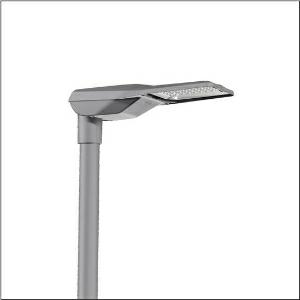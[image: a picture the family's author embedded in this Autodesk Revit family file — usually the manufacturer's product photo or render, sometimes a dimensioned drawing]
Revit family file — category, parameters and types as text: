
# Revit family: streetlight_sl_21_iq_mini___st1_5a_5xe2p41g08hb_3230
name_source: partatom
category: Lighting Fixtures
units: mm (PartAtom-declared; Revit-internal decimal feet)

## family parameters
Cut with Voids When Loaded = No
Host = Face
Light Source = No
Part Type = Normal
Room Calculation Point = No
Round Connector Dimension = Use Diameter
Shared = No

## types (1)
- --- (1 x LED, 9690 lm, 70.9 W, 4000K)
    Apparent Load = 71 VA
    CIE Flux Codes = 22 53 95 100 100
    Color Rendering = 70
    Color Temperature = 4000K
    Default Elevation = 1800 mm
    Description = Streetlight SL 21 mini, mast luminaire, primary light control with lens, of PMMA, primary optical cover: cover, of toughened safety glass, transparent, light distribution: ST1.5a, light emission: direct distribution, primary light characteristic: asymmetric, installation type: post-top, side-entry, LED, High Power LED, rated luminous flux: 9.690lm, luminous efficacy: 137lm/W, light colour: 740, colour temperature: 4000K, control gear: ECG iQ, control: Street-Remote, Auto-Match, Temp-Guard, Lumen-Switch, Night-Set, Smart-Wire, Light-Fading, Desk-Remote (wireless, voltage-free reading and setting of iQ features in the workshop via application-optimized NFC function/RFID function), optimised constant luminous flux control (CLO 2.0), mains connection: 220..240V, AC, 50/60Hz, start of lifetime: 71W, end of lifetime: 75W, reduction: 31W, luminaire housing, of diecast aluminium, powder-coated, Siteco® metallic grey (DB 702S), corrosivity category C5 according to DIN EN ISO 12944, length: 628mm, width: 235mm, height: 110mm, spigot size: 60/76mm (post-top) and 42/60/76mm (side-entry), mast flange for spigot size: 42mm: 5XC10008XM4, 60mm: 5XC10008XM2, 76/60mm: 5XC10108XM1, protection rating (complete): IP66, insulation class (complete): insulation class II (safety insulation), certification: CE, ENEC, VDE, impact resistance: IK09, permissible operating ambient temperature for outdoor applications: -40..+50°C, standard-compliant lighting for roads and squares, packaging unit: 1 piece

Light Distribution: ST1.5a
    Height = 110 mm
    Lamp = 1 x LED
    Lamp Light Flux = 9690 lm
    Lamp Power = 70.9 W
    Lamp count = 1
    Length = 625 mm
    Luminous efficacy = 137 lm/W
    Manufacturer = Siteco
    ModVariant = No
    Model = 5XE2P41G08HB
    Number of Poles = 1
    OnlyDefault = Yes
    Power Factor = 1
    Product Name = Streetlight SL 21 iQ mini | ST1.5a
    Product group = mast luminaire | pylon top
    ProductGroupID = 6100
    Protection Class = Protection class II
    Protection Degree = IP 66
    RLX_Detail_Level = 1
    RlxData = <blob elided: 95629 chars, md5=6103194e>
    Socket = socket
    Standby Power = 0 W
    System Light Flux = 9690 lm
    System Power = 71 W
    Type Comments = factory setting: luminous flux: 100 % | dim-lin: 254 | 711 mA
    Type Image = l_1003519.jpg
    URL = http://relux.com
    VarID = @adj_068315
    Voltage = 0 V
    Weight = 0.00 kg
    Width = 234 mm

## geometry (parser evidence)
native form markers: Blend x4, Sweep x11
no freeform markers — native parametric forms only
